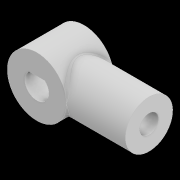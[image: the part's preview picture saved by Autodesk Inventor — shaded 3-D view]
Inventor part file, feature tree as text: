
AUTODESK INVENTOR PART (.ipt)
format: ipt  version: 2020 (Build 240168000, 168)  size: 166,400 bytes
history: native  units: mm
features: sketch x3, extrude x2, plane x1, hole x1, fillet x1, projected_geometry x1
ambient origin geometry x8: Origin, YZ Plane, XZ Plane, XY Plane, X Axis, Y Axis, Z Axis, Center Point
bodies: Solid1 (feature_tree)
feature tree (9):
  extrude  "Extrusion1"  Depth=0.5mm
  plane  "Work Plane1"
  extrude  "Extrusion2"  Depth=8.0mm
  hole  "Hole1"  [1 undecoded]
  fillet  "Fillet1"  Radius=0.5mm
  sketch  "Sketch1"  dims[d0=4.1mm d2=0.5mm]
  sketch  "Sketch2"  dims[d3=8.0mm d4=0.0mm d5=8.0mm]
  projected_geometry  "Projected Loop1"
  sketch  "Sketch3"  dims[d6=10.0mm d7=2.0mm d8=0.0mm d9=0.0mm d10=3.2mm d11=9.95mm d12=3.023mm d13=2.0mm d14=14.3117mm d15=176.2125mm d16=0.0mm d17=10.0mm d18=0.5mm]
note: 1 required parameter value undecoded (feature->parameter linkage not recoverable at this tier; creation-order binding heuristic only, values carry confidence <= 0.55)
